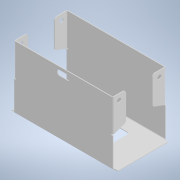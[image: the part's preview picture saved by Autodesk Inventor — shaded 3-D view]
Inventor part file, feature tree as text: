
AUTODESK INVENTOR PART (.ipt)
format: ipt  version: 2022 (Build 260153000, 153)  size: 393,728 bytes
history: native  units: mm
features: other x18, sketch x6, projected_geometry x6, reference x2, fillet x1, mirror x1
ambient origin geometry x8: Origin, YZ Plane, XZ Plane, XY Plane, X Axis, Y Axis, Z Axis, Center Point
bodies: Body1 (feature_tree)
feature tree (34):
  other  "Твердое тело1"
  other  "Грань1"
  other  "Фланец2"
  other  "Фланец5"
  fillet  "Сопряжение2"  Radius=0.5mm
  mirror  "Зеркальное отражение2"
  sketch  "Эскиз1"
  other  "Пластина1"
  sketch  "Эскиз3"
  other  "Пластина3"
  other  "Сгиб2"
  other  "УглСтык2"
  sketch  "Эскиз4"
  sketch  "Эскиз10"
  projected_geometry  "Спроецированная петля2"
  sketch  "Эскиз11"
  other  "Пластина6"
  other  "Сгиб5"
  other  "УглСтык5"
  projected_geometry  "Спроецированная петля3"
  sketch  "Эскиз12"
  reference  "Ссылка3"
  reference  "Ссылка4"
  projected_geometry  "Спроецированная петля4"
  projected_geometry  "Спроецированная петля5"
  projected_geometry  "Спроецированная петля6"
  other  "Вырез1"
  other  "Вырез5"
  other  "Вырез6"
  other  "Определение1"
  other  "<userpath>\Documents\Git\MZCAT_battery\FastBattery2.iam"
  other  "FastBattery2.iam"
  other  "akkum_base2_2:1"
  projected_geometry  "Спроецированная петля1"
